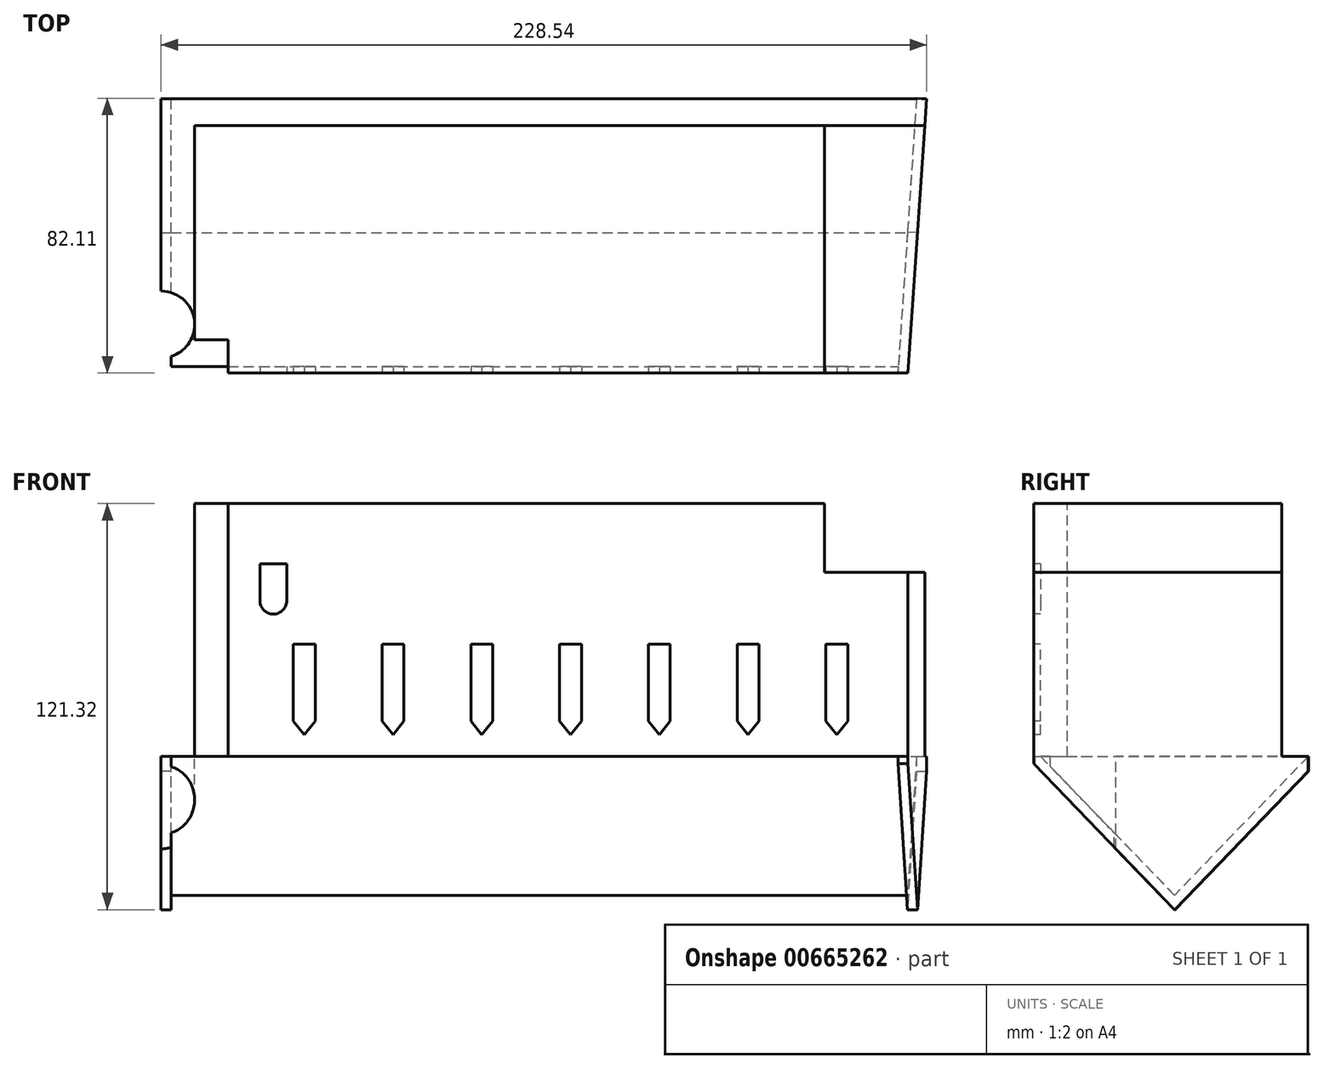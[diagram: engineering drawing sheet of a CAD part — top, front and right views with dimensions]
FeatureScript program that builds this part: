
annotation { "Feature Type Name" : "Feature", "Feature Type Description" : "" }
export const myFeature = defineFeature(function(context is Context, id is Id, definition is map)
    precondition{}
    {
        {
            var Q0;
            Q0=qCreatedBy(makeId("Top.planeOp"),FACE);
            var sketch = newSketch(context, id + "F0", { "sketchPlane" : qUnion([Q0])});
            skLineSegment(sketch, "E0", {"start": v(0, 0) * mm, "end": v(0, 64) * mm});
            skLineSegment(sketch, "E1", {"start": v(0, 64) * mm, "end": v(188, 64) * mm});
            skLineSegment(sketch, "E2", {"start": v(188, 64) * mm, "end": v(188, -10) * mm});
            skLineSegment(sketch, "E3", {"start": v(188, -10) * mm, "end": v(10, -10) * mm});
            skLineSegment(sketch, "E4", {"start": v(10, -10) * mm, "end": v(10, 0) * mm});
            skLineSegment(sketch, "E5", {"start": v(10, 0) * mm, "end": v(0, 0) * mm});
            skSolve(sketch);
        }
        {
            var Q0;
            Q0=makeQuery(id+"F0.imprint","IMPRINT",FACE,{"disambiguationData":[TD([[makeQuery(id+"F0.imprint","IMPRINT",EDGE,{"derivedFrom":sQuery(id+"F0.wireOp",EDGE,"E0")}),-1.0]])]});
            extrude(context, id + "F1", {"entities" : qUnion([Q0]), "oppositeDirection" : true, "depth" : 20.5 * mm, "offsetDistance" : 25 * mm});
        }
        {
            var Q0;
            Q0=makeQuery(id+"F1.opExtrude","CAP_FACE",FACE,{"disambiguationData":[OSD([sQuery(id+"F0.wireOp",EDGE,"E0"),sQuery(id+"F0.wireOp",EDGE,"E1"),sQuery(id+"F0.wireOp",EDGE,"E2"),sQuery(id+"F0.wireOp",EDGE,"E3"),sQuery(id+"F0.wireOp",EDGE,"E4"),sQuery(id+"F0.wireOp",EDGE,"E5")])],"isStart":false});
            var sketch = newSketch(context, id + "F2", { "sketchPlane" : qUnion([Q0])});
            skLineSegment(sketch, "E6.0.0", {"start": v(10, 0) * mm, "end": v(0, 0) * mm});
            skLineSegment(sketch, "E6.0.1", {"start": v(0, 0) * mm, "end": v(0, -64) * mm});
            skLineSegment(sketch, "E6.0.2", {"start": v(0, -64) * mm, "end": v(188, -64) * mm});
            skLineSegment(sketch, "E6.0.4", {"start": v(188, 10) * mm, "end": v(10, 10) * mm});
            skLineSegment(sketch, "E6.0.5", {"start": v(10, 10) * mm, "end": v(10, 0) * mm});
            skLineSegment(sketch, "E7", {"start": v(188, 10) * mm, "end": v(213, 10) * mm});
            skLineSegment(sketch, "E8", {"start": v(213, 10) * mm, "end": v(218, -64) * mm});
            skLineSegment(sketch, "E9", {"start": v(218, -64) * mm, "end": v(188, -64) * mm});
            skSolve(sketch);
        }
        {
            var Q0;
            Q0=makeQuery(id+"F2.imprint","IMPRINT",FACE,{"disambiguationData":[TD([[makeQuery(id+"F2.imprint","IMPRINT",EDGE,{"derivedFrom":sQuery(id+"F2.wireOp",EDGE,"E7")}),-1.0]])]});
            var Q1;
            Q1=makeQuery(id+"F2.imprint","IMPRINT",FACE,{"disambiguationData":[TD([[makeQuery(id+"F2.imprint","IMPRINT",EDGE,{"derivedFrom":sQuery(id+"F2.wireOp",EDGE,"E6.0.0")}),1.0]])]});
            extrude(context, id + "F3", {"entities" : qUnion([Q0, Q1]), "operationType" : NewBodyOperationType.ADD, "depth" : 55 * mm, "offsetDistance" : 25 * mm});
        }
        {
            var Q0;
            Q0=makeQuery(id+"F3.boolean.opBoolean","MERGE",FACE,{"derivedFrom":[makeQuery(id+"F1.opExtrude","SWEPT_FACE",FACE,{"disambiguationData":[OSD([sQuery(id+"F0.wireOp",EDGE,"E0")])]}),makeQuery(id+"F3.opExtrude","SWEPT_FACE",FACE,{"disambiguationData":[OSD([sQuery(id+"F2.wireOp",EDGE,"E6.0.1")])]})]});
            var sketch = newSketch(context, id + "F4", { "sketchPlane" : qUnion([Q0])});
            skLineSegment(sketch, "E10.0", {"start": v(0, -75.5) * mm, "end": v(-64, -75.5) * mm});
            skLineSegment(sketch, "E11", {"start": v(-64, -75.5) * mm, "end": v(-72, -75.5) * mm, "construction": true});
            skLineSegment(sketch, "E12", {"start": v(0, -75.5) * mm, "end": v(8, -75.5) * mm});
            skLineSegment(sketch, "E13", {"start": v(8, -75.5) * mm, "end": v(-32, -117) * mm});
            skLineSegment(sketch, "E14", {"start": v(-32, -117) * mm, "end": v(-72, -75.5) * mm});
            skLineSegment(sketch, "E15", {"start": v(8, -75.5) * mm, "end": v(-72, -75.5) * mm});
            skSolve(sketch);
        }
        {
            var Q0;
            {var subQ5=sQuery(id+"F4.wireOp",EDGE,"E13");Q0=makeQuery(id+"F4.imprint","IMPRINT",FACE,{"disambiguationData":[TD([[makeQuery(id+"F4.imprint","IMPRINT",EDGE,{"derivedFrom":subQ5}),-1.0]])]});}
            var Q1;
            Q1=makeQuery(id+"F3.opExtrude","SWEPT_FACE",FACE,{"disambiguationData":[OSD([sQuery(id+"F2.wireOp",EDGE,"E8")])]});
            var Q2;
            Q2=makeQuery(id+"F1.opExtrude","SWEPT_BODY",BODY,{"disambiguationData":[OSD([sQuery(id+"F0.wireOp",EDGE,"E0"),sQuery(id+"F0.wireOp",EDGE,"E1"),sQuery(id+"F0.wireOp",EDGE,"E2"),sQuery(id+"F0.wireOp",EDGE,"E3"),sQuery(id+"F0.wireOp",EDGE,"E4"),sQuery(id+"F0.wireOp",EDGE,"E5")])]});
            extrude(context, id + "F5", {"entities" : qUnion([Q0]), "depth" : 7 * mm, "offsetDistance" : 25 * mm, "hasSecondDirection" : true, "secondDirectionBound" : SecondDirectionBoundingType.UP_TO_SURFACE, "secondDirectionOppositeDirection" : true, "secondDirectionDepth" : 201 * mm, "secondDirectionBoundEntityFace" : qUnion([Q1]), "secondDirectionBoundEntityBody" : qUnion([Q2])});
        }
        {
            var Q0;
            Q0=makeQuery(id+"F5.opExtrude","CAP_FACE",FACE,{"disambiguationData":[OSD([sQuery(id+"F4.wireOp",EDGE,"E13"),sQuery(id+"F4.wireOp",EDGE,"E14"),sQuery(id+"F4.wireOp",EDGE,"E15")])],"isStart":false});
            var sketch = newSketch(context, id + "F6", { "sketchPlane" : qUnion([Q0])});
            skLineSegment(sketch, "E16.1", {"start": v(-14, -102.65) * mm, "end": v(-32, -121.32) * mm});
            skLineSegment(sketch, "E17", {"start": v(-14, -75.5) * mm, "end": v(-14, -102.65) * mm});
            skLineSegment(sketch, "E18", {"start": v(-32, -121.32) * mm, "end": v(-72, -79.82) * mm});
            skLineSegment(sketch, "E19", {"start": v(-14, -75.5) * mm, "end": v(-72, -75.5) * mm});
            skLineSegment(sketch, "E20", {"start": v(-72, -75.5) * mm, "end": v(-72, -79.82) * mm});
            skPoint(sketch, "E21.orphan", {"position": v(-76.17, -75.5) * mm});
            skSolve(sketch);
        }
        {
            var Q0;
            Q0=makeQuery(id+"F6.imprint","IMPRINT",FACE,{"disambiguationData":[TD([[makeQuery(id+"F6.imprint","IMPRINT",EDGE,{"derivedFrom":sQuery(id+"F6.wireOp",EDGE,"E16.0")}),-1.0]])]});
            var Q1;
            {var subQ0=makeQuery(id+"Fvq21iVMnHBKpmn_1.opExtrude","CAP_EDGE",EDGE,{"disambiguationData":[OSD([sQuery(id+"F4.wireOp",EDGE,"E14")])],"isStart":true});Q1=makeQuery(id+"F6.imprint","IMPRINT",FACE,{"disambiguationData":[TD([[makeQuery(id+"F6.imprint","IMPRINT",EDGE,{"derivedFrom":subQ0}),-1.0]])]});}
            var Q2;
            {var subQ2=sQuery(id+"F6.wireOp",EDGE,"E16.1");Q2=makeQuery(id+"F6.imprint","IMPRINT",FACE,{"disambiguationData":[TD([[makeQuery(id+"F6.imprint","IMPRINT",EDGE,{"derivedFrom":subQ2}),-1.0]])]});}
            var Q3;
            {var subQ5=makeQuery(id+"F5.opExtrude","CAP_EDGE",EDGE,{"disambiguationData":[OSD([sQuery(id+"F4.wireOp",EDGE,"E14")])],"isStart":false});Q3=makeQuery(id+"F6.imprint","IMPRINT",FACE,{"disambiguationData":[TD([[makeQuery(id+"F6.imprint","IMPRINT",EDGE,{"derivedFrom":subQ5}),-1.0]])]});}
            extrude(context, id + "F7", {"entities" : qUnion([Q0, Q1, Q2, Q3]), "operationType" : NewBodyOperationType.ADD, "depth" : 3 * mm, "offsetDistance" : 25 * mm});
        }
        {
            var Q0;
            {var subQ0=sQuery(id+"F2.wireOp",EDGE,"E8");Q0=makeQuery(id+"Fvq21iVMnHBKpmn_1.boolean.opBoolean","MERGE",FACE,{"derivedFrom":[makeQuery(id+"F3.opExtrude","SWEPT_FACE",FACE,{"disambiguationData":[OSD([subQ0])]}),makeQuery(id+"Fvq21iVMnHBKpmn_1.opExtrude","CAP_FACE",FACE,{"disambiguationData":[OSD([subQ0])],"isStart":false})]});}
            var sketch = newSketch(context, id + "F8", { "sketchPlane" : qUnion([Q0])});
            skLineSegment(sketch, "E22", {"start": v(86.47, -75.5) * mm, "end": v(4.38, -75.5) * mm});
            skLineSegment(sketch, "E23", {"start": v(4.38, -75.5) * mm, "end": v(4.38, -77.74) * mm});
            skLineSegment(sketch, "E24", {"start": v(90.74, -75.5) * mm, "end": v(90.74, -75.5) * mm});
            skLineSegment(sketch, "E25", {"start": v(86.47, -79.92) * mm, "end": v(46.48, -121.32) * mm});
            skLineSegment(sketch, "E26", {"start": v(46.48, -121.32) * mm, "end": v(4.38, -77.74) * mm});
            skLineSegment(sketch, "E27", {"start": v(4.38, -75.5) * mm, "end": v(86.47, -75.5) * mm});
            skLineSegment(sketch, "E28", {"start": v(86.47, -75.5) * mm, "end": v(86.47, -79.92) * mm});
            skSolve(sketch);
        }
        {
            var Q0;
            {var subQ0=sQuery(id+"F8.wireOp",EDGE,"E23");Q0=makeQuery(id+"F8.imprint","IMPRINT",FACE,{"disambiguationData":[TD([[makeQuery(id+"F8.imprint","IMPRINT",EDGE,{"derivedFrom":subQ0}),1.0]])]});}
            var Q1;
            {var subQ1=sQuery(id+"F2.wireOp",EDGE,"E8");var subQ2=makeQuery(id+"F3.opExtrude","SWEPT_FACE",FACE,{"disambiguationData":[OSD([subQ1])]});var subQ5=makeQuery(id+"Fvq21iVMnHBKpmn_1.opExtrude","TWEAK_EDGE",EDGE,{"derivedFrom":[subQ2,makeQuery(id+"F4.imprint","IMPRINT",EDGE,{"derivedFrom":sQuery(id+"F4.wireOp",EDGE,"E13")})]});Q1=makeQuery(id+"F8.imprint","IMPRINT",FACE,{"disambiguationData":[TD([[makeQuery(id+"F8.imprint","IMPRINT",EDGE,{"derivedFrom":subQ5}),1.0]])]});}
            extrude(context, id + "F9", {"entities" : qUnion([Q0, Q1]), "operationType" : NewBodyOperationType.ADD, "oppositeDirection" : true, "depth" : 3 * mm, "offsetDistance" : 25 * mm});
        }
        {
            var Q0;
            Q0=makeQuery(id+"F9.boolean.opBoolean","MERGE",FACE,{"derivedFrom":[makeQuery(id+"F7.boolean.opBoolean","MERGE",FACE,{"derivedFrom":[makeQuery(id+"F5.opExtrude","SWEPT_FACE",FACE,{"disambiguationData":[OSD([sQuery(id+"F4.wireOp",EDGE,"E15")])]}),makeQuery(id+"F7.opExtrude","SWEPT_FACE",FACE,{"disambiguationData":[OSD([sQuery(id+"F6.wireOp",EDGE,"E19")])]})]}),makeQuery(id+"F9.opExtrude","SWEPT_FACE",FACE,{"disambiguationData":[OSD([sQuery(id+"F8.wireOp",EDGE,"E27")])]})]});
            var sketch = newSketch(context, id + "F10", { "sketchPlane" : qUnion([Q0])});
            skCircle(sketch, "E29", {"center": v(-10, 4.5) * mm, "radius": 10 * mm});
            skSolve(sketch);
        }
        {
            var Q0;
            {var subQ0=sQuery(id+"F10.wireOp",EDGE,"E29");var subQ1=makeQuery(id+"F5.opExtrude","CAP_EDGE",EDGE,{"disambiguationData":[OSD([sQuery(id+"F4.wireOp",EDGE,"E15")])],"isStart":false});var subQ2=makeQuery(id+"F10.imprint","INTERSECT",VERTEX,{"disambiguationData":[OD(0.0)],"derivedFrom":[subQ1,subQ0]});Q0=makeQuery(id+"F10.imprint","IMPRINT",FACE,{"disambiguationData":[TD([[makeQuery(id+"F10.imprint","IMPRINT",EDGE,{"disambiguationData":[TD([[subQ2,-1.0]])],"derivedFrom":subQ0}),1.0]])]});}
            extrude(context, id + "F11", {"entities" : qUnion([Q0]), "operationType" : NewBodyOperationType.REMOVE, "oppositeDirection" : true, "depth" : 39.5 * mm, "offsetDistance" : 25 * mm});
        }
        {
            var Q0;
            Q0=makeQuery(id+"F3.boolean.opBoolean","MERGE",FACE,{"derivedFrom":[makeQuery(id+"F1.opExtrude","SWEPT_FACE",FACE,{"disambiguationData":[OSD([sQuery(id+"F0.wireOp",EDGE,"E3")])]}),makeQuery(id+"F3.opExtrude","SWEPT_FACE",FACE,{"disambiguationData":[OSD([sQuery(id+"F2.wireOp",EDGE,"E6.0.4"),sQuery(id+"F2.wireOp",EDGE,"E7")])]})]});
            var sketch = newSketch(context, id + "F12", { "sketchPlane" : qUnion([Q0])});
            skLineSegment(sketch, "E30.bottom", {"start": v(195, -65) * mm, "end": v(188.5, -65) * mm});
            skLineSegment(sketch, "E30.top", {"start": v(195, -42) * mm, "end": v(188.5, -42) * mm});
            skLineSegment(sketch, "E30.left", {"start": v(195, -65) * mm, "end": v(195, -42) * mm});
            skLineSegment(sketch, "E30.right", {"start": v(188.5, -65) * mm, "end": v(188.5, -42) * mm});
            skPoint(sketch, "E31.1.internal.snap0", {"position": v(191.75, -65) * mm});
            skLineSegment(sketch, "E32", {"start": v(195, -65) * mm, "end": v(191.75, -69) * mm});
            skLineSegment(sketch, "E33", {"start": v(191.75, -69) * mm, "end": v(188.5, -65) * mm});
            skPoint(sketch, "E34.1.0.0", {"position": v(165.25, -65) * mm});
            skLineSegment(sketch, "E34.1.0.1", {"start": v(168.5, -65) * mm, "end": v(168.5, -42) * mm});
            skLineSegment(sketch, "E34.1.0.2", {"start": v(162, -65) * mm, "end": v(162, -42) * mm});
            skLineSegment(sketch, "E34.1.0.3", {"start": v(168.5, -42) * mm, "end": v(162, -42) * mm});
            skLineSegment(sketch, "E34.1.0.4", {"start": v(168.5, -65) * mm, "end": v(162, -65) * mm});
            skLineSegment(sketch, "E34.1.0.5", {"start": v(168.5, -65) * mm, "end": v(165.25, -69) * mm});
            skLineSegment(sketch, "E34.1.0.6", {"start": v(165.25, -69) * mm, "end": v(162, -65) * mm});
            skPoint(sketch, "E34.2.0.0", {"position": v(138.75, -65) * mm});
            skLineSegment(sketch, "E34.2.0.1", {"start": v(142, -65) * mm, "end": v(142, -42) * mm});
            skLineSegment(sketch, "E34.2.0.2", {"start": v(135.5, -65) * mm, "end": v(135.5, -42) * mm});
            skLineSegment(sketch, "E34.2.0.3", {"start": v(142, -42) * mm, "end": v(135.5, -42) * mm});
            skLineSegment(sketch, "E34.2.0.4", {"start": v(142, -65) * mm, "end": v(135.5, -65) * mm});
            skLineSegment(sketch, "E34.2.0.5", {"start": v(142, -65) * mm, "end": v(138.75, -69) * mm});
            skLineSegment(sketch, "E34.2.0.6", {"start": v(138.75, -69) * mm, "end": v(135.5, -65) * mm});
            skPoint(sketch, "E34.3.0.0", {"position": v(112.25, -65) * mm});
            skLineSegment(sketch, "E34.3.0.1", {"start": v(115.5, -65) * mm, "end": v(115.5, -42) * mm});
            skLineSegment(sketch, "E34.3.0.2", {"start": v(109, -65) * mm, "end": v(109, -42) * mm});
            skLineSegment(sketch, "E34.3.0.3", {"start": v(115.5, -42) * mm, "end": v(109, -42) * mm});
            skLineSegment(sketch, "E34.3.0.4", {"start": v(115.5, -65) * mm, "end": v(109, -65) * mm});
            skLineSegment(sketch, "E34.3.0.5", {"start": v(115.5, -65) * mm, "end": v(112.25, -69) * mm});
            skLineSegment(sketch, "E34.3.0.6", {"start": v(112.25, -69) * mm, "end": v(109, -65) * mm});
            skPoint(sketch, "E34.4.0.0", {"position": v(85.75, -65) * mm});
            skLineSegment(sketch, "E34.4.0.1", {"start": v(89, -65) * mm, "end": v(89, -42) * mm});
            skLineSegment(sketch, "E34.4.0.2", {"start": v(82.5, -65) * mm, "end": v(82.5, -42) * mm});
            skLineSegment(sketch, "E34.4.0.3", {"start": v(89, -42) * mm, "end": v(82.5, -42) * mm});
            skLineSegment(sketch, "E34.4.0.4", {"start": v(89, -65) * mm, "end": v(82.5, -65) * mm});
            skLineSegment(sketch, "E34.4.0.5", {"start": v(89, -65) * mm, "end": v(85.75, -69) * mm});
            skLineSegment(sketch, "E34.4.0.6", {"start": v(85.75, -69) * mm, "end": v(82.5, -65) * mm});
            skPoint(sketch, "E34.5.0.0", {"position": v(59.25, -65) * mm});
            skLineSegment(sketch, "E34.5.0.1", {"start": v(62.5, -65) * mm, "end": v(62.5, -42) * mm});
            skLineSegment(sketch, "E34.5.0.2", {"start": v(56, -65) * mm, "end": v(56, -42) * mm});
            skLineSegment(sketch, "E34.5.0.3", {"start": v(62.5, -42) * mm, "end": v(56, -42) * mm});
            skLineSegment(sketch, "E34.5.0.4", {"start": v(62.5, -65) * mm, "end": v(56, -65) * mm});
            skLineSegment(sketch, "E34.5.0.5", {"start": v(62.5, -65) * mm, "end": v(59.25, -69) * mm});
            skLineSegment(sketch, "E34.5.0.6", {"start": v(59.25, -69) * mm, "end": v(56, -65) * mm});
            skPoint(sketch, "E34.6.0.0", {"position": v(32.75, -65) * mm});
            skLineSegment(sketch, "E34.6.0.1", {"start": v(36, -65) * mm, "end": v(36, -42) * mm});
            skLineSegment(sketch, "E34.6.0.2", {"start": v(29.5, -65) * mm, "end": v(29.5, -42) * mm});
            skLineSegment(sketch, "E34.6.0.3", {"start": v(36, -42) * mm, "end": v(29.5, -42) * mm});
            skLineSegment(sketch, "E34.6.0.4", {"start": v(36, -65) * mm, "end": v(29.5, -65) * mm});
            skLineSegment(sketch, "E34.6.0.5", {"start": v(36, -65) * mm, "end": v(32.75, -69) * mm});
            skLineSegment(sketch, "E34.6.0.6", {"start": v(32.75, -69) * mm, "end": v(29.5, -65) * mm});
            skLineSegment(sketch, "E34.direction1", {"start": v(191.75, -69) * mm, "end": v(165.25, -69) * mm, "construction": true});
            skLineSegment(sketch, "E35.bottom", {"start": v(19.5, -18) * mm, "end": v(27.5, -18) * mm});
            skLineSegment(sketch, "E35.left", {"start": v(19.5, -18) * mm, "end": v(19.5, -29) * mm});
            skLineSegment(sketch, "E35.right", {"start": v(27.5, -18) * mm, "end": v(27.5, -29) * mm});
            skArc(sketch, "E36", {"start": v(19.5, -29) * mm, "mid": v(23.5, -33) * mm, "end": v(27.5, -29) * mm});
            skSolve(sketch);
        }
        {
            var Q0;
            Q0=makeQuery(id+"F12.imprint","IMPRINT",FACE,{"disambiguationData":[TD([[makeQuery(id+"F12.imprint","IMPRINT",EDGE,{"derivedFrom":sQuery(id+"F12.wireOp",EDGE,"E34.2.0.1")}),1.0]])]});
            var Q1;
            Q1=makeQuery(id+"F12.imprint","IMPRINT",FACE,{"disambiguationData":[TD([[makeQuery(id+"F12.imprint","IMPRINT",EDGE,{"derivedFrom":sQuery(id+"F12.wireOp",EDGE,"E34.3.0.1")}),1.0]])]});
            var Q2;
            Q2=makeQuery(id+"F12.imprint","IMPRINT",FACE,{"disambiguationData":[TD([[makeQuery(id+"F12.imprint","IMPRINT",EDGE,{"derivedFrom":sQuery(id+"F12.wireOp",EDGE,"E34.4.0.1")}),1.0]])]});
            var Q3;
            Q3=makeQuery(id+"F12.imprint","IMPRINT",FACE,{"disambiguationData":[TD([[makeQuery(id+"F12.imprint","IMPRINT",EDGE,{"derivedFrom":sQuery(id+"F12.wireOp",EDGE,"E34.5.0.1")}),1.0]])]});
            var Q4;
            Q4=makeQuery(id+"F12.imprint","IMPRINT",FACE,{"disambiguationData":[TD([[makeQuery(id+"F12.imprint","IMPRINT",EDGE,{"derivedFrom":sQuery(id+"F12.wireOp",EDGE,"E34.6.0.1")}),1.0]])]});
            var Q5;
            Q5=makeQuery(id+"F12.imprint","IMPRINT",FACE,{"disambiguationData":[TD([[makeQuery(id+"F12.imprint","IMPRINT",EDGE,{"derivedFrom":sQuery(id+"F12.wireOp",EDGE,"E34.6.0.4")}),1.0]])]});
            var Q6;
            Q6=makeQuery(id+"F12.imprint","IMPRINT",FACE,{"disambiguationData":[TD([[makeQuery(id+"F12.imprint","IMPRINT",EDGE,{"derivedFrom":sQuery(id+"F12.wireOp",EDGE,"E34.5.0.4")}),1.0]])]});
            var Q7;
            Q7=makeQuery(id+"F12.imprint","IMPRINT",FACE,{"disambiguationData":[TD([[makeQuery(id+"F12.imprint","IMPRINT",EDGE,{"derivedFrom":sQuery(id+"F12.wireOp",EDGE,"E34.4.0.4")}),1.0]])]});
            var Q8;
            Q8=makeQuery(id+"F12.imprint","IMPRINT",FACE,{"disambiguationData":[TD([[makeQuery(id+"F12.imprint","IMPRINT",EDGE,{"derivedFrom":sQuery(id+"F12.wireOp",EDGE,"E34.3.0.4")}),1.0]])]});
            var Q9;
            Q9=makeQuery(id+"F12.imprint","IMPRINT",FACE,{"disambiguationData":[TD([[makeQuery(id+"F12.imprint","IMPRINT",EDGE,{"derivedFrom":sQuery(id+"F12.wireOp",EDGE,"E34.2.0.4")}),1.0]])]});
            var Q10;
            Q10=makeQuery(id+"F12.imprint","IMPRINT",FACE,{"disambiguationData":[TD([[makeQuery(id+"F12.imprint","IMPRINT",EDGE,{"derivedFrom":sQuery(id+"F12.wireOp",EDGE,"E34.1.0.1")}),1.0]])]});
            var Q11;
            Q11=makeQuery(id+"F12.imprint","IMPRINT",FACE,{"disambiguationData":[TD([[makeQuery(id+"F12.imprint","IMPRINT",EDGE,{"derivedFrom":sQuery(id+"F12.wireOp",EDGE,"E34.1.0.4")}),1.0]])]});
            var Q12;
            Q12=makeQuery(id+"F12.imprint","IMPRINT",FACE,{"disambiguationData":[TD([[makeQuery(id+"F12.imprint","IMPRINT",EDGE,{"derivedFrom":sQuery(id+"F12.wireOp",EDGE,"E30.bottom")}),1.0]])]});
            var Q13;
            Q13=makeQuery(id+"F12.imprint","IMPRINT",FACE,{"disambiguationData":[TD([[makeQuery(id+"F12.imprint","IMPRINT",EDGE,{"derivedFrom":sQuery(id+"F12.wireOp",EDGE,"E30.bottom")}),-1.0]])]});
            var Q14;
            Q14=makeQuery(id+"F12.imprint","IMPRINT",FACE,{"disambiguationData":[TD([[makeQuery(id+"F12.imprint","IMPRINT",EDGE,{"derivedFrom":sQuery(id+"F12.wireOp",EDGE,"E35.bottom")}),-1.0]])]});
            extrude(context, id + "F13", {"entities" : qUnion([Q0, Q1, Q2, Q3, Q4, Q5, Q6, Q7, Q8, Q9, Q10, Q11, Q12, Q13, Q14]), "operationType" : NewBodyOperationType.REMOVE, "oppositeDirection" : true, "depth" : 2 * mm, "offsetDistance" : 25 * mm});
        }
    });
